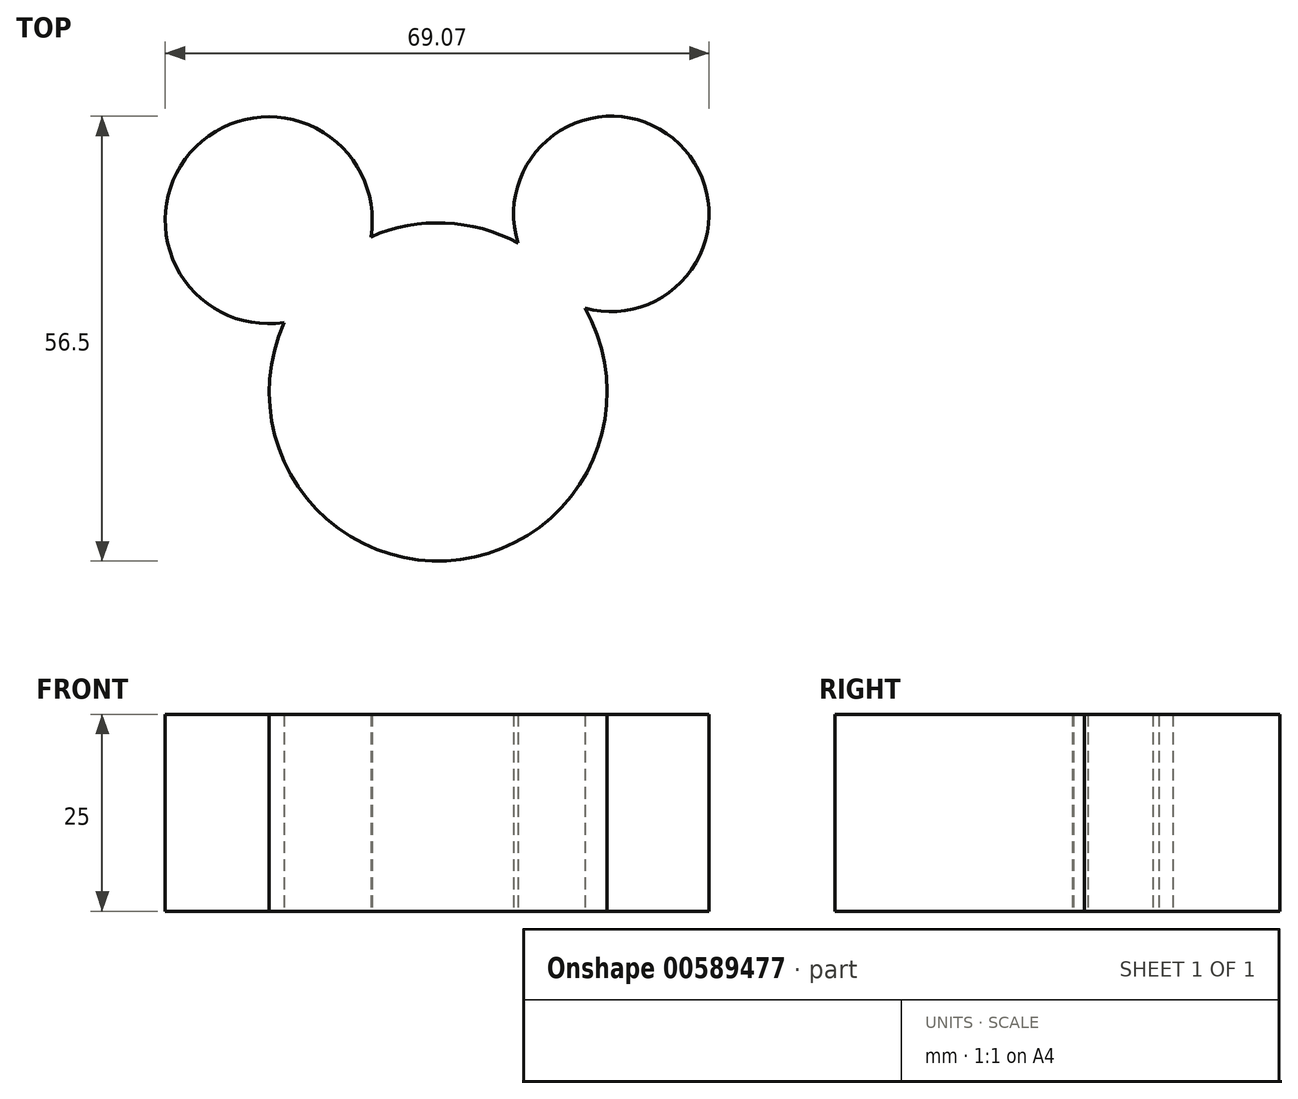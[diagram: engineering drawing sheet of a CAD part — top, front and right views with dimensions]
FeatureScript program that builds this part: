
annotation { "Feature Type Name" : "Feature", "Feature Type Description" : "" }
export const myFeature = defineFeature(function(context is Context, id is Id, definition is map)
    precondition{}
    {
        {
            var Q0;
            Q0=qCreatedBy(makeId("Top.planeOp"),FACE);
            var sketch = newSketch(context, id + "F0", { "sketchPlane" : qUnion([Q0])});
            skCircle(sketch, "E0", {"center": v(-35.13, 7.5) * mm, "radius": 13.14 * mm});
            skCircle(sketch, "E1", {"center": v(-13.6, -14.3) * mm, "radius": 21.47 * mm});
            skCircle(sketch, "E2", {"center": v(8.4, 8.31) * mm, "radius": 12.4 * mm});
            skSolve(sketch);
        }
        {
            var Q0;
            Q0 = qSketchRegion(id + "F0", true);
            extrude(context, id + "F1", {"entities" : qUnion([Q0]), "depth" : 25 * mm, "offsetDistance" : 25 * mm});
        }
    });
